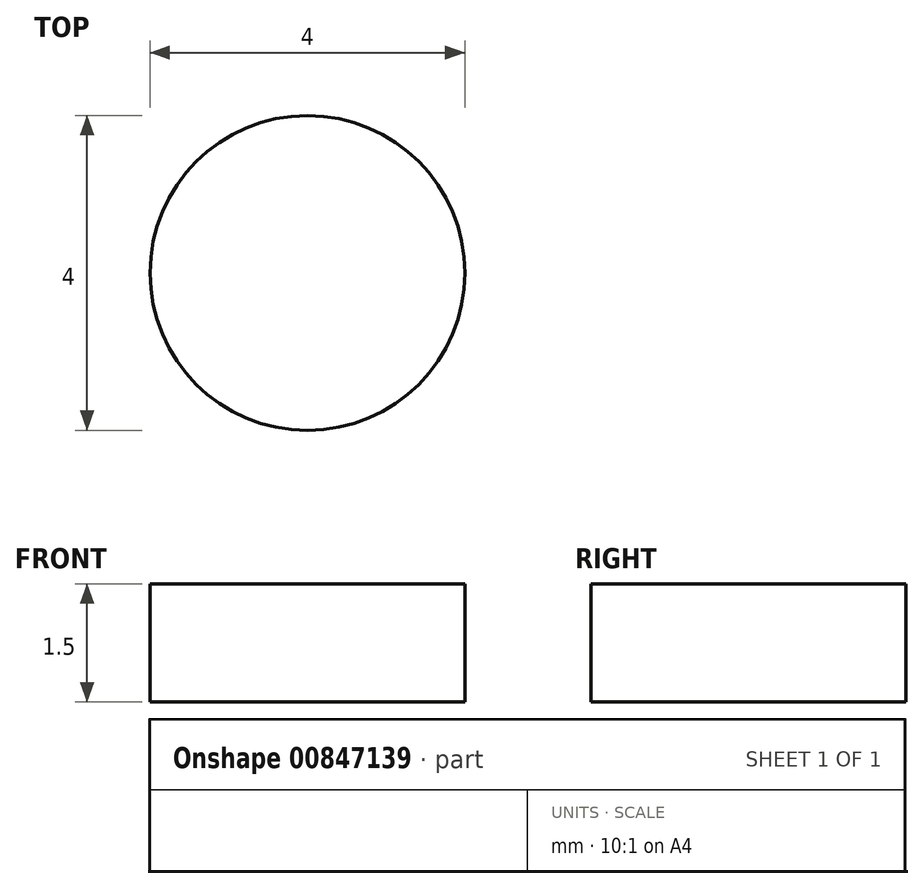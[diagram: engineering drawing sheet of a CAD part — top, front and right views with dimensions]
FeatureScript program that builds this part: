
annotation { "Feature Type Name" : "Feature", "Feature Type Description" : "" }
export const myFeature = defineFeature(function(context is Context, id is Id, definition is map)
    precondition{}
    {
        {
            var Q0;
            Q0=qCreatedBy(makeId("Top.planeOp"),FACE);
            var sketch = newSketch(context, id + "F0", { "sketchPlane" : qUnion([Q0])});
            skCircle(sketch, "E0", {"center": v(0, 0) * mm, "radius": 2 * mm});
            skSolve(sketch);
        }
        {
            var Q0;
            Q0=makeQuery(id+"F0.imprint","IMPRINT",FACE,{"disambiguationData":[TD([[makeQuery(id+"F0.imprint","IMPRINT",EDGE,{"derivedFrom":sQuery(id+"F0.wireOp",EDGE,"E0")}),1.0]])]});
            extrude(context, id + "F1", {"entities" : qUnion([Q0]), "depth" : 1.5 * mm, "offsetDistance" : 25 * mm});
        }
    });
